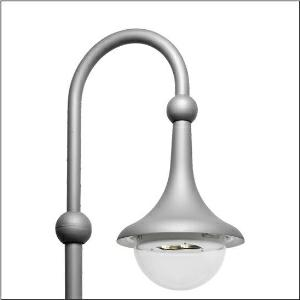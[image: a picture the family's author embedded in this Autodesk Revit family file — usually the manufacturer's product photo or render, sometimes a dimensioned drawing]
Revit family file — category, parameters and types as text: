
# Revit family: grosse_glocke_iq___st1_2a_5xa1565m1f108_263f
name_source: partatom
category: Lighting Fixtures
units: mm (PartAtom-declared; Revit-internal decimal feet)

## family parameters
Cut with Voids When Loaded = No
Host = Face
Light Source = No
Part Type = Normal
Room Calculation Point = No
Round Connector Dimension = Use Diameter
Shared = No

## types (1)
- --- (1 x LED, 4470 lm, 34.3 W, 2700K)
    Apparent Load = 34 VA
    CIE Flux Codes = 28 66 95 100 100
    Color Rendering = 70
    Color Temperature = 2700K
    Default Elevation = 1800 mm
    Description = Large Bell iQ, mast luminaire, primary light control with 3 zone facetted reflector, of plastic, silver coated, primary optical cover: enclosure, of PMMA, transparent, light distribution: ST1.2a, light emission: direct distribution, primary light characteristic: asymmetric, installation type: suspended mounting, High Power LED, rated luminous flux: 4.470lm, luminous efficacy: 130lm/W, light colour: 727, colour temperature: 2700K, control gear: iQ Street-Remote, control: optimised constant luminous flux control (CLO 2.0), Desk-Remote (wireless, voltage-free reading and setting of iQ features in the workshop via application-optimized NFC function/RFID function), Light-Fading, Smart-Wire, Night-Set, Lumen-Switch, Temp-Guard, Auto-Match, Street-Remote, pre-setting: logarithmic dimming characteristic, mains connection: 230..240V, AC, 50/60Hz, start of lifetime: 34W, end of service life: 38W, reduction: 16W, luminaire housing, bell-shaped, of glass-fibre reinforced polyester, coated, Siteco® metallic grey (DB 702S), please order curved mast extension separately, diameter: 530mm, height: 695mm, mounting height: 4..6m, protection rating (complete): IP54, insulation class (complete): insulation class II (safety insulation), certification: CE, ENEC, VDE, impact resistance: IK08, standard-compliant lighting for roads and squares, packaging unit: 1 piece

Light Distribution: ST1.2a
    Height = 695 mm
    Lamp = 1 x LED
    Lamp Light Flux = 4470 lm
    Lamp Power = 34.3 W
    Lamp count = 1
    Length = 530 mm
    Luminous efficacy = 130 lm/W
    Manufacturer = Siteco
    ModVariant = No
    Model = 5XA1565M1F108
    Mounting Place = Pole
    Mounting Type = Pole annexe
    Number of Poles = 1
    OnlyDefault = Yes
    Power Factor = 1
    Product Name = Große Glocke iQ | ST1.2a
    Product group = mast luminaire | pylon annexe
    ProductGroupID = 6200
    Protection Class = Protection class II
    Protection Degree = IP 54
    RLX_Detail_Level = 1
    RLX_Emergency_Light_Flux = 0 lm
    RLX_Emergency_Type = 0
    RLX_Emergency_Type_DB = No
    RlxData = <blob elided: 85437 chars, md5=3db00188>
    Socket = socket
    Standby Power = 0 W
    System Light Flux = 4470 lm
    System Power = 34 W
    Type Comments = factory setting: luminous flux: 100 % | dim-lin: 254 | 640 mA
    Type Image = l_1347688.jpg
    URL = http://relux.com
    VarID = @adj_067837
    Voltage = 0 V
    Weight = 0.00 kg
    Width = 0 mm  [stored 0 ft]

note: [stored X ft] marks values corroborated as IEEE doubles in the binary element streams (Revit-internal decimal feet)

## geometry (parser evidence)
native form markers: Blend x4, Sweep x9
no freeform markers — native parametric forms only
